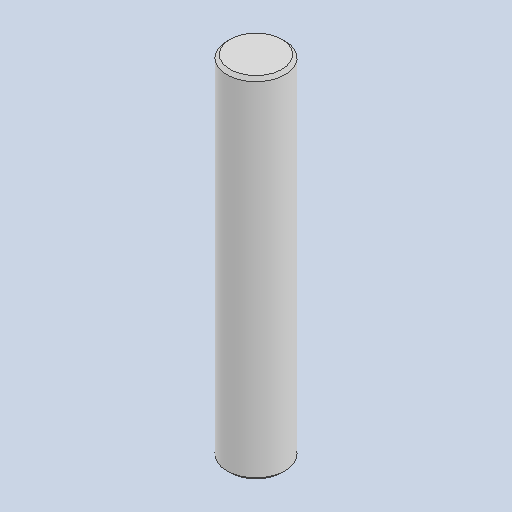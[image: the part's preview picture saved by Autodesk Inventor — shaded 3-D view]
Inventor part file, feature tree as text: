
AUTODESK INVENTOR PART (.ipt)
format: ipt  version: 2022 (Build 260153000, 153)  size: 74,240 bytes
history: native  units: in
note: dims shown in document units (in); Inventor stores cm internally (conversion verified against a paired STEP export)
features: chamfer x1
ambient origin geometry x8: Origin, YZ Plane, XZ Plane, XY Plane, X Axis, Y Axis, Z Axis, Center Point
bodies: Solid1 (feature_tree)
feature tree (1):
  chamfer  "Chamfer1"  [1 undecoded]
note: 1 required parameter value undecoded (feature->parameter linkage not recoverable at this tier; creation-order binding heuristic only, values carry confidence <= 0.55)
